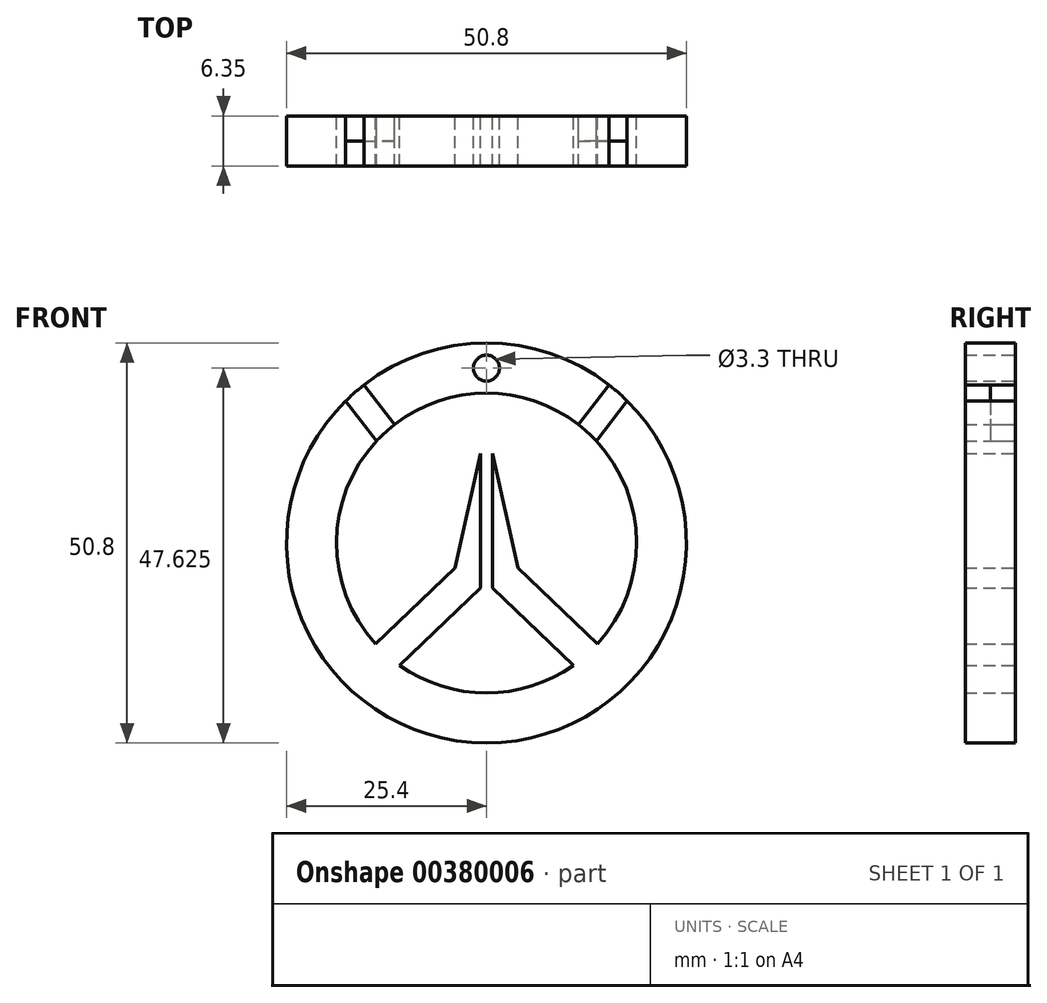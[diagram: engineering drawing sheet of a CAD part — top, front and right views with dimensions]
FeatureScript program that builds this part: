
annotation { "Feature Type Name" : "Feature", "Feature Type Description" : "" }
export const myFeature = defineFeature(function(context is Context, id is Id, definition is map)
    precondition{}
    {
        {
            var Q0;
            Q0=qCreatedBy(makeId("Front.planeOp"),FACE);
            var sketch = newSketch(context, id + "F0", { "sketchPlane" : qUnion([Q0])});
            skCircle(sketch, "E0", {"center": v(0, 0) * mm, "radius": 25.4 * mm});
            skCircle(sketch, "E1", {"center": v(0, 0) * mm, "radius": 19.05 * mm});
            skLineSegment(sketch, "E2", {"start": v(-17.87, 18.05) * mm, "end": v(-13.94, 12.98) * mm});
            skLineSegment(sketch, "E3", {"start": v(-15.58, 20.06) * mm, "end": v(-11.68, 15.05) * mm});
            skLineSegment(sketch, "E4", {"start": v(11.68, 15.05) * mm, "end": v(15.58, 20.06) * mm});
            skLineSegment(sketch, "E5", {"start": v(17.87, 18.05) * mm, "end": v(13.94, 12.98) * mm});
            skLineSegment(sketch, "E6", {"start": v(-14.08, -12.83) * mm, "end": v(-3.98, -3.18) * mm});
            skLineSegment(sketch, "E7", {"start": v(-11.03, -15.53) * mm, "end": v(-0.76, -5.73) * mm});
            skPoint(sketch, "E8", {"position": v(0, -19.05) * mm});
            skPoint(sketch, "E9", {"position": v(0, 19.05) * mm});
            skLineSegment(sketch, "E10", {"start": v(11.03, -15.53) * mm, "end": v(0.76, -5.72) * mm});
            skLineSegment(sketch, "E11", {"start": v(14.08, -12.83) * mm, "end": v(3.98, -3.18) * mm});
            skLineSegment(sketch, "E12", {"start": v(-0.76, -5.73) * mm, "end": v(-0.76, 11.39) * mm});
            skLineSegment(sketch, "E13", {"start": v(0.76, -5.72) * mm, "end": v(0.76, 11.36) * mm});
            skLineSegment(sketch, "E14", {"start": v(-3.98, -3.18) * mm, "end": v(-0.76, 11.39) * mm});
            skLineSegment(sketch, "E15", {"start": v(3.98, -3.18) * mm, "end": v(0.76, 11.36) * mm});
            skCircle(sketch, "E16", {"center": v(0, 22.23) * mm, "radius": 1.65 * mm});
            skSolve(sketch);
        }
        {
            var Q0;
            {var subQ0=sQuery(id+"F0.wireOp",EDGE,"E10");Q0=makeQuery(id+"F0.imprint","IMPRINT",FACE,{"disambiguationData":[TD([[makeQuery(id+"F0.imprint","IMPRINT",EDGE,{"derivedFrom":subQ0}),-1.0]])]});}
            var Q1;
            {var subQ1=sQuery(id+"F0.wireOp",EDGE,"E6");Q1=makeQuery(id+"F0.imprint","IMPRINT",FACE,{"disambiguationData":[TD([[makeQuery(id+"F0.imprint","IMPRINT",EDGE,{"derivedFrom":subQ1}),-1.0]])]});}
            var Q2;
            {var subQ3=sQuery(id+"F0.wireOp",EDGE,"E2");Q2=makeQuery(id+"F0.imprint","IMPRINT",FACE,{"disambiguationData":[TD([[makeQuery(id+"F0.imprint","IMPRINT",EDGE,{"derivedFrom":subQ3}),-1.0]])]});}
            var Q3;
            {var subQ0=sQuery(id+"F0.wireOp",EDGE,"E3");Q3=makeQuery(id+"F0.imprint","IMPRINT",FACE,{"disambiguationData":[TD([[makeQuery(id+"F0.imprint","IMPRINT",EDGE,{"derivedFrom":subQ0}),1.0]])]});}
            extrude(context, id + "F1", {"entities" : qUnion([Q0, Q1, Q2, Q3]), "depth" : 6.35 * mm});
        }
        {
            var Q0;
            {var subQ0=sQuery(id+"F0.wireOp",EDGE,"E2");Q0=makeQuery(id+"F0.imprint","IMPRINT",FACE,{"disambiguationData":[TD([[makeQuery(id+"F0.imprint","IMPRINT",EDGE,{"derivedFrom":subQ0}),1.0]])]});}
            var Q1;
            {var subQ0=sQuery(id+"F0.wireOp",EDGE,"E4");Q1=makeQuery(id+"F0.imprint","IMPRINT",FACE,{"disambiguationData":[TD([[makeQuery(id+"F0.imprint","IMPRINT",EDGE,{"derivedFrom":subQ0}),-1.0]])]});}
            extrude(context, id + "F2", {"entities" : qUnion([Q0, Q1]), "depth" : 3.17 * mm});
        }
    });
